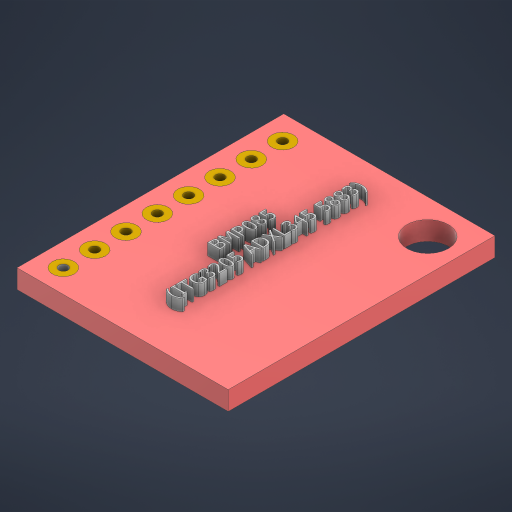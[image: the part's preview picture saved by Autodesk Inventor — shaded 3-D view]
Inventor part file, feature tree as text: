
AUTODESK INVENTOR PART (.ipt)
format: ipt  version: 2023 (Build 270158000, 158)  size: 1,043,456 bytes
history: native  units: mm
features: sketch x5, extrude x2, hole x2, pattern_linear x1, emboss x1, projected_geometry x1
ambient origin geometry x8: Origin, YZ Plane, XZ Plane, XY Plane, X Axis, Y Axis, Z Axis, Center Point
bodies: Solid1 (feature_tree)
feature tree (12):
  extrude  "Extrusion1"  Depth=21.62mm
  hole  "Hole1"  [1 undecoded]
  hole  "Hole2"  [1 undecoded]
  extrude  "Extrusion2"  Depth=1.77mm
  pattern_linear  "Rectangular Pattern1"  Spacing1=0.001mm  [1 undecoded]
  emboss  "Emboss1"
  sketch  "Sketch1"  dims[d0=17.12mm d1=21.62mm]
  sketch  "Sketch2"  dims[d2=1.53mm d3=0.0mm d4=2.665mm]
  sketch  "Sketch3"  dims[d5=2.785mm]
  sketch  "Sketch5"  dims[d6=3.37mm d7=6.0mm d8=4.0mm d9=2.0mm d10=90.0deg d11=8.0mm d12=20.594885mm d13=1.875mm]
  projected_geometry  "Projected Loop1"
  sketch  "Sketch6"  dims[d14=1.875mm d15=0.73mm d16=6.0mm d17=4.0mm d18=2.0mm d19=90.0deg d20=8.0mm d21=20.594885mm d22=1.77mm d23=0.001mm d24=0.0mm d25=80.0mm d27=2.54mm d28=0.93mm d29=0.0mm]
note: 3 required parameter values undecoded (feature->parameter linkage not recoverable at this tier; creation-order binding heuristic only, values carry confidence <= 0.55)
